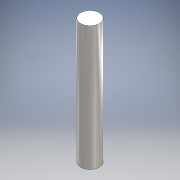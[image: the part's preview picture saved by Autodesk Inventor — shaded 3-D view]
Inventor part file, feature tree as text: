
AUTODESK INVENTOR PART (.ipt)
format: ipt  version: 2016 (Build 200138000, 138)  size: 90,112 bytes
history: native  units: mm
features: other x1, extrude x1, sketch x1
ambient origin geometry x8: Origin, YZ Plane, XZ Plane, XY Plane, X Axis, Y Axis, Z Axis, Center Point
bodies: Body1 (feature_tree)
feature tree (3):
  other  "ソリッド1"
  extrude  "押し出し1"  Depth=6.0mm
  sketch  "スケッチ1"
